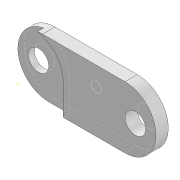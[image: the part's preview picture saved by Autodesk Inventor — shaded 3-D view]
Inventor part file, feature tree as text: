
AUTODESK INVENTOR PART (.ipt)
format: ipt  version: 2021 (Build 250183000, 183)  size: 158,720 bytes
history: native  units: mm
features: extrude x4, sketch x4, projected_geometry x1
ambient origin geometry x8: Origin, YZ Plane, XZ Plane, XY Plane, X Axis, Y Axis, Z Axis, Center Point
bodies: Solid1 (feature_tree)
feature tree (9):
  extrude  "Extrusion1"  Depth=10.0mm
  sketch  "Sketch4"  dims[d15=10.0mm d16=10.0mm]
  extrude  "Extrusion3"  Depth=10.0mm
  extrude  "Extrusion4"  Depth=15.0mm
  extrude  "Extrusion5"  TaperAngle=0.0deg  [1 undecoded]
  sketch  "Sketch1"  dims[d1=30.0mm d14=10.0mm]
  projected_geometry  "Projected Loop2"
  sketch  "Sketch5"  dims[d17=50.0mm d18=15.0mm]
  sketch  "Sketch6"  dims[d19=3.0mm d20=0.0mm d21=15.0mm d24=15.0mm d25=3.0mm d26=0.0mm d27=3.0mm d30=5.0mm d31=0.1mm d32=0.0mm d33=35.0mm d34=10.0mm d36=15.0mm d37=0.1mm d38=0.0mm d28=0.5mm d29=0.872665mm]
note: 1 required parameter value undecoded (feature->parameter linkage not recoverable at this tier; creation-order binding heuristic only, values carry confidence <= 0.55)
